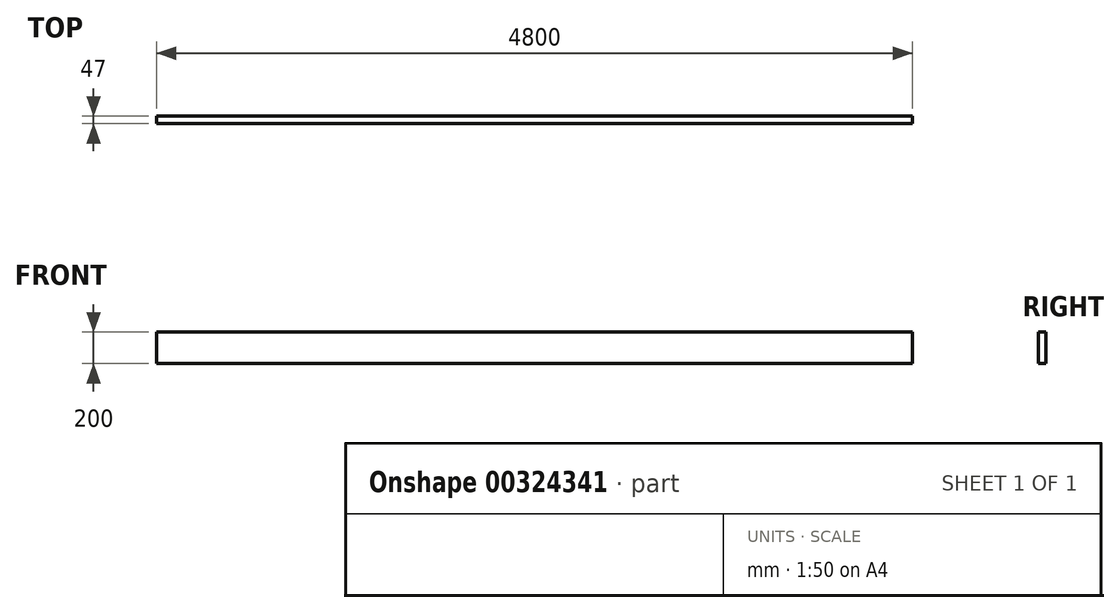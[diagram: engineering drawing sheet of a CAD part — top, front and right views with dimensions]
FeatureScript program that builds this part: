
annotation { "Feature Type Name" : "Feature", "Feature Type Description" : "" }
export const myFeature = defineFeature(function(context is Context, id is Id, definition is map)
    precondition{}
    {
        {
            var Q0;
            Q0=qCreatedBy(makeId("Top.planeOp"),FACE);
            var sketch = newSketch(context, id + "F0", { "sketchPlane" : qUnion([Q0])});
            skLineSegment(sketch, "E0.bottom", {"start": v(2400, -23.5) * mm, "end": v(-2400, -23.5) * mm});
            skLineSegment(sketch, "E0.top", {"start": v(2400, 23.5) * mm, "end": v(-2400, 23.5) * mm});
            skLineSegment(sketch, "E0.left", {"start": v(2400, -23.5) * mm, "end": v(2400, 23.5) * mm});
            skLineSegment(sketch, "E0.right", {"start": v(-2400, -23.5) * mm, "end": v(-2400, 23.5) * mm});
            skPoint(sketch, "E0.middle", {"position": v(0, 0) * mm});
            skSolve(sketch);
        }
        {
            var Q0;
            Q0=makeQuery(id+"F0.imprint","IMPRINT",FACE,{"disambiguationData":[TD([[makeQuery(id+"F0.imprint","IMPRINT",EDGE,{"derivedFrom":sQuery(id+"F0.wireOp",EDGE,"E0.bottom")}),-1.0]])]});
            extrude(context, id + "F1", {"entities" : qUnion([Q0]), "depth" : 200 * mm});
        }
        {
            var Q0;
            Q0=makeQuery(id+"F1.opExtrude","SWEPT_FACE",FACE,{"disambiguationData":[OSD([sQuery(id+"F0.wireOp",EDGE,"E0.right")])]});
            var sketch = newSketch(context, id + "F2", { "sketchPlane" : qUnion([Q0])});
            skLineSegment(sketch, "E1", {"start": v(0, 0) * mm, "end": v(0, -60) * mm, "construction": true});
            skLineSegment(sketch, "E2", {"start": v(0, -60) * mm, "end": v(-25.03, -60) * mm});
            skSolve(sketch);
        }
        {
            var Q0;
            Q0=makeQuery(id+"F1.opExtrude","SWEPT_FACE",FACE,{"disambiguationData":[OSD([sQuery(id+"F0.wireOp",EDGE,"E0.bottom")])]});
            var sketch = newSketch(context, id + "F3", { "sketchPlane" : qUnion([Q0])});
            skPoint(sketch, "E3.0", {"position": v(-2400, -60) * mm});
            skLineSegment(sketch, "E4.0", {"start": v(-2400, 0) * mm, "end": v(-2400, -60) * mm});
            skLineSegment(sketch, "E5.0.0", {"start": v(2400, 0) * mm, "end": v(-2400, 0) * mm});
            skLineSegment(sketch, "E5.0.1", {"start": v(-2400, 0) * mm, "end": v(-2400, 200) * mm});
            skLineSegment(sketch, "E5.0.2", {"start": v(-2400, 200) * mm, "end": v(2400, 200) * mm});
            skLineSegment(sketch, "E5.0.3", {"start": v(2400, 200) * mm, "end": v(2400, 0) * mm});
            skLineSegment(sketch, "E6", {"start": v(-2400, -60) * mm, "end": v(2100, 0) * mm});
            skSolve(sketch);
        }
        {
            var Q0;
            Q0=makeQuery(id+"F1.opExtrude","CAP_FACE",FACE,{"disambiguationData":[OSD([sQuery(id+"F0.wireOp",EDGE,"E0.bottom"),sQuery(id+"F0.wireOp",EDGE,"E0.top"),sQuery(id+"F0.wireOp",EDGE,"E0.left"),sQuery(id+"F0.wireOp",EDGE,"E0.right")])],"isStart":true});
            var sketch = newSketch(context, id + "F4", { "sketchPlane" : qUnion([Q0])});
            skLineSegment(sketch, "E7.0", {"start": v(-2400, 23.5) * mm, "end": v(2100, 23.5) * mm});
            skLineSegment(sketch, "E8", {"start": v(2100, 23.5) * mm, "end": v(2100, -23.5) * mm});
            skSolve(sketch);
        }
    });
